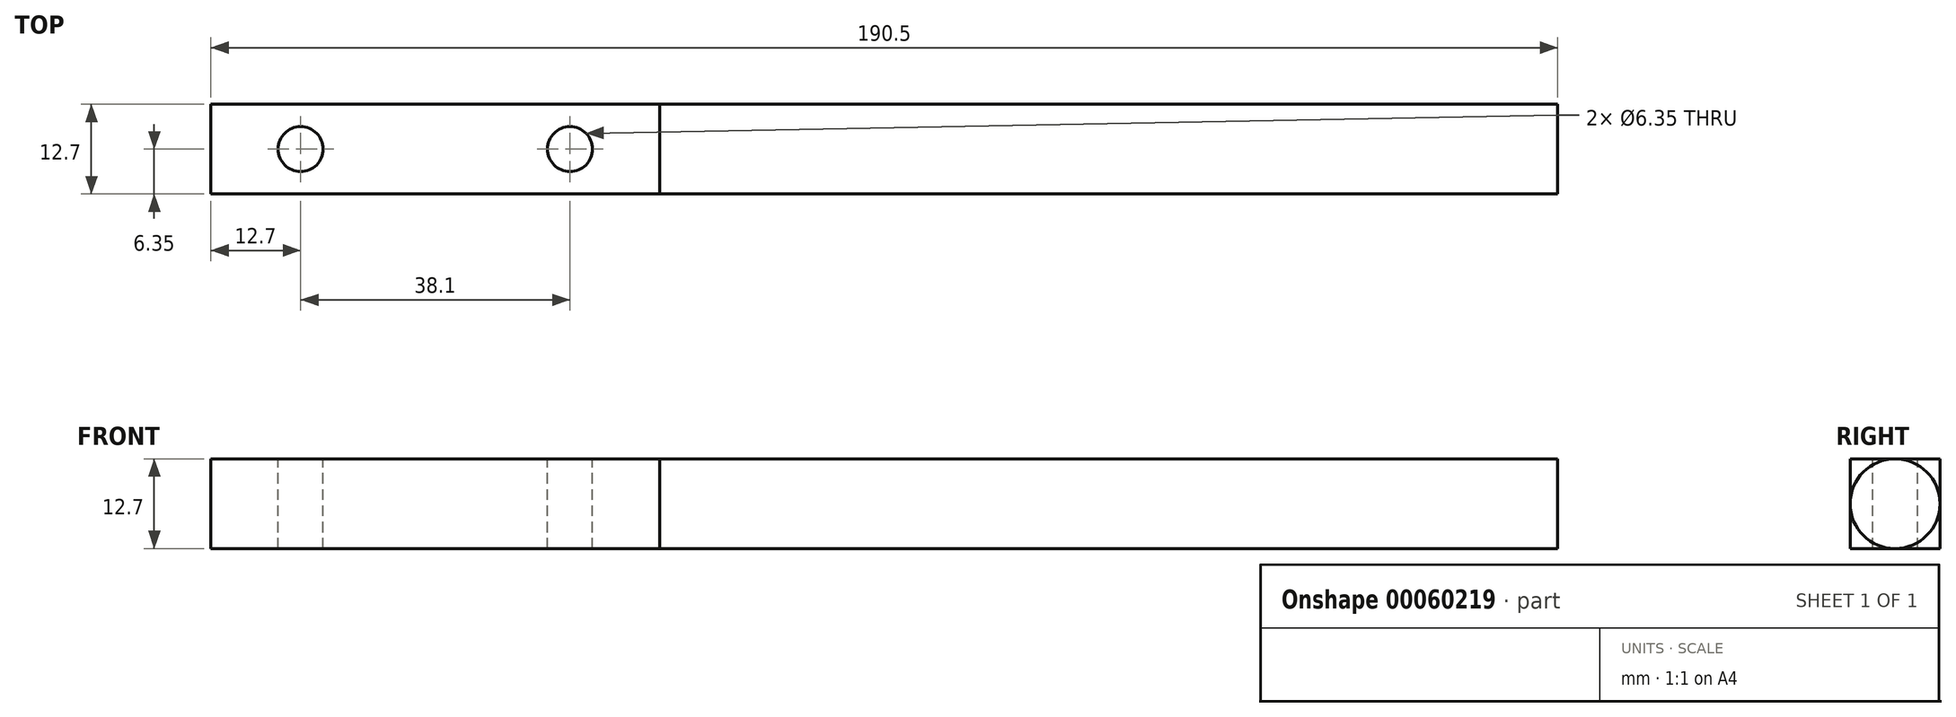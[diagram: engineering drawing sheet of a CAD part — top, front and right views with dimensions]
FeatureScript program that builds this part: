
annotation { "Feature Type Name" : "Feature", "Feature Type Description" : "" }
export const myFeature = defineFeature(function(context is Context, id is Id, definition is map)
    precondition{}
    {
        {
            var Q0;
            Q0=qCreatedBy(makeId("Front.planeOp"),FACE);
            var sketch = newSketch(context, id + "F0", { "sketchPlane" : qUnion([Q0])});
            skLineSegment(sketch, "E0.bottom", {"start": v(0, 0) * mm, "end": v(127, 0) * mm});
            skLineSegment(sketch, "E0.top", {"start": v(0, 6.35) * mm, "end": v(127, 6.35) * mm});
            skLineSegment(sketch, "E0.left", {"start": v(0, 0) * mm, "end": v(0, 6.35) * mm});
            skLineSegment(sketch, "E0.right", {"start": v(127, 0) * mm, "end": v(127, 6.35) * mm});
            skSolve(sketch);
        }
        {
            var Q0;
            Q0 = qSketchRegion(id + "F0", true);
            var Q1;
            Q1=sQuery(id+"F0.wireOp",EDGE,"E0.bottom");
            revolve(context, id + "F1", {"entities" : qUnion([Q0]), "axis" : qUnion([Q1]), "revolveType" : RevolveType.FULL});
        }
        {
            var Q0;
            Q0=makeQuery(id+"F1.opRevolve","SWEPT_FACE",FACE,{"disambiguationData":[OSD([sQuery(id+"F0.wireOp",EDGE,"E0.left")])]});
            var sketch = newSketch(context, id + "F2", { "sketchPlane" : qUnion([Q0])});
            skLineSegment(sketch, "E1.rect.bottom", {"start": v(6.35, -6.35) * mm, "end": v(-6.35, -6.35) * mm});
            skLineSegment(sketch, "E1.rect.top", {"start": v(6.35, 6.35) * mm, "end": v(-6.35, 6.35) * mm});
            skLineSegment(sketch, "E1.rect.left", {"start": v(6.35, -6.35) * mm, "end": v(6.35, 6.35) * mm});
            skLineSegment(sketch, "E1.rect.right", {"start": v(-6.35, -6.35) * mm, "end": v(-6.35, 6.35) * mm});
            skPoint(sketch, "E1.rect.middle", {"position": v(0, 0) * mm});
            skSolve(sketch);
        }
        {
            var Q0;
            Q0 = qSketchRegion(id + "F2", true);
            extrude(context, id + "F3", {"entities" : qUnion([Q0]), "operationType" : NewBodyOperationType.ADD, "depth" : 63.5 * mm});
        }
        {
            var Q0;
            Q0=makeQuery(id+"F3.opExtrude","SWEPT_FACE",FACE,{"disambiguationData":[OSD([sQuery(id+"F2.wireOp",EDGE,"E1.rect.top")])]});
            var sketch = newSketch(context, id + "F4", { "sketchPlane" : qUnion([Q0])});
            skCircle(sketch, "E2", {"center": v(-50.8, 0) * mm, "radius": 3.17 * mm});
            skCircle(sketch, "E3", {"center": v(-12.7, 0) * mm, "radius": 3.18 * mm});
            skSolve(sketch);
        }
        {
            var Q0;
            Q0=makeQuery(id+"F4.imprint","IMPRINT",FACE,{"disambiguationData":[TD([[makeQuery(id+"F4.imprint","IMPRINT",EDGE,{"derivedFrom":sQuery(id+"F4.wireOp",EDGE,"E2")}),1.0]])]});
            var Q1;
            Q1=makeQuery(id+"F4.imprint","IMPRINT",FACE,{"disambiguationData":[TD([[makeQuery(id+"F4.imprint","IMPRINT",EDGE,{"derivedFrom":sQuery(id+"F4.wireOp",EDGE,"E3")}),1.0]])]});
            extrude(context, id + "F5", {"entities" : qUnion([Q0, Q1]), "operationType" : NewBodyOperationType.REMOVE, "oppositeDirection" : true, "depth" : 127 * mm});
        }
    });
